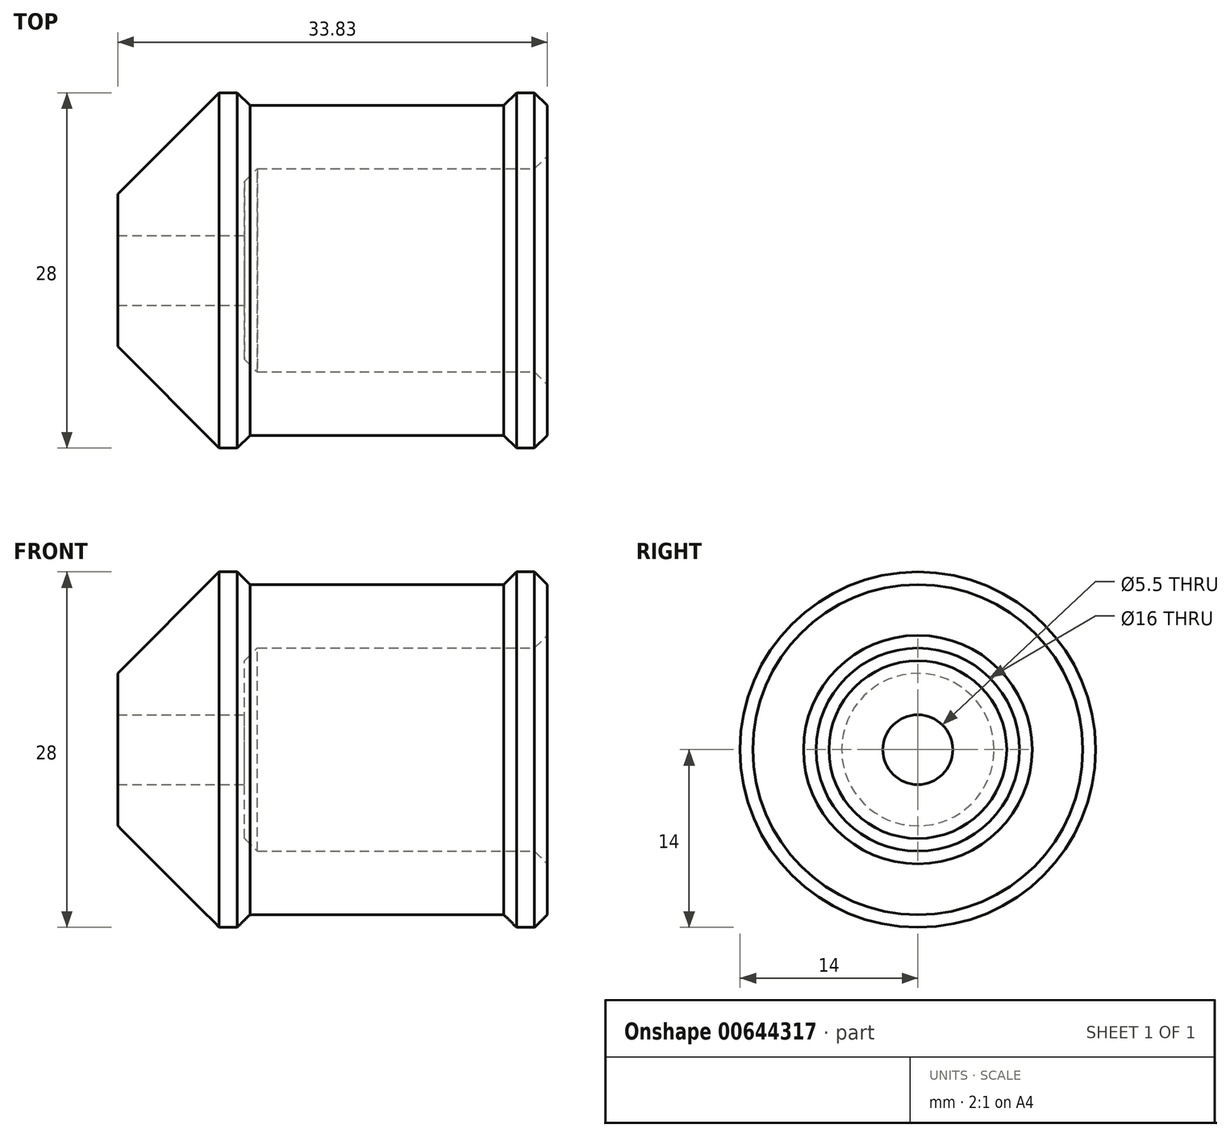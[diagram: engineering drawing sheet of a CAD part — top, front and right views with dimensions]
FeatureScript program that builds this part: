
annotation { "Feature Type Name" : "Feature", "Feature Type Description" : "" }
export const myFeature = defineFeature(function(context is Context, id is Id, definition is map)
    precondition{}
    {
        {
            var Q0;
            Q0=qCreatedBy(makeId("Front.planeOp"),FACE);
            var sketch = newSketch(context, id + "F0", { "sketchPlane" : qUnion([Q0])});
            skLineSegment(sketch, "E0", {"start": v(-10, 2.75) * mm, "end": v(0, 2.75) * mm});
            skLineSegment(sketch, "E1", {"start": v(0, 2.75) * mm, "end": v(0, 8) * mm});
            skLineSegment(sketch, "E2", {"start": v(0, 8) * mm, "end": v(23.83, 8) * mm});
            skLineSegment(sketch, "E3", {"start": v(23.83, 8) * mm, "end": v(23.83, 13) * mm});
            skLineSegment(sketch, "E4", {"start": v(23.83, 13) * mm, "end": v(-3, 13) * mm, "construction": true});
            skLineSegment(sketch, "E5", {"start": v(-3, 13) * mm, "end": v(-10, 6) * mm});
            skLineSegment(sketch, "E6", {"start": v(-10, 6) * mm, "end": v(-10, 2.75) * mm});
            skLineSegment(sketch, "E7", {"start": v(-24.63, 0) * mm, "end": v(31.55, 0) * mm, "construction": true});
            skLineSegment(sketch, "E8", {"start": v(-3, 13) * mm, "end": v(-2, 14) * mm});
            skLineSegment(sketch, "E9", {"start": v(-2, 14) * mm, "end": v(-0.59, 14) * mm});
            skLineSegment(sketch, "E10", {"start": v(-0.59, 14) * mm, "end": v(0.41, 13) * mm});
            skLineSegment(sketch, "E11", {"start": v(0.41, 13) * mm, "end": v(20.41, 13) * mm});
            skLineSegment(sketch, "E12", {"start": v(20.41, 13) * mm, "end": v(21.41, 14) * mm});
            skLineSegment(sketch, "E13", {"start": v(21.41, 14) * mm, "end": v(22.83, 14) * mm});
            skLineSegment(sketch, "E14", {"start": v(22.83, 14) * mm, "end": v(23.83, 13) * mm});
            skSolve(sketch);
        }
        {
            var Q0;
            Q0 = qConstructionFilter(qBodyType(qCreatedBy(id + "F0" ,EDGE), BodyType.WIRE), ConstructionObject.NO);
            var Q1;
            Q1=sQuery(id+"F0.wireOp",EDGE,"E7");
            revolve(context, id + "F1", {"bodyType" : ToolBodyType.SURFACE, "surfaceEntities" : qUnion([Q0]), "axis" : qUnion([Q1]), "revolveType" : RevolveType.FULL});
        }
        {
            var Q0;
            Q0=makeQuery(id+"F1.opRevolve","SWEPT_EDGE",EDGE,{"disambiguationData":[OSD([sQuery(id+"F0.wireOp",VERTEX,"E3.start")])]});
            var Q1;
            Q1=makeQuery(id+"F1.opRevolve","SWEPT_EDGE",EDGE,{"disambiguationData":[OSD([sQuery(id+"F0.wireOp",VERTEX,"E2.start")])]});
            chamfer(context, id + "F2", {"entities" : qUnion([Q0, Q1]), "width" : 1 * mm, "tangentPropagation" : true});
        }
    });
